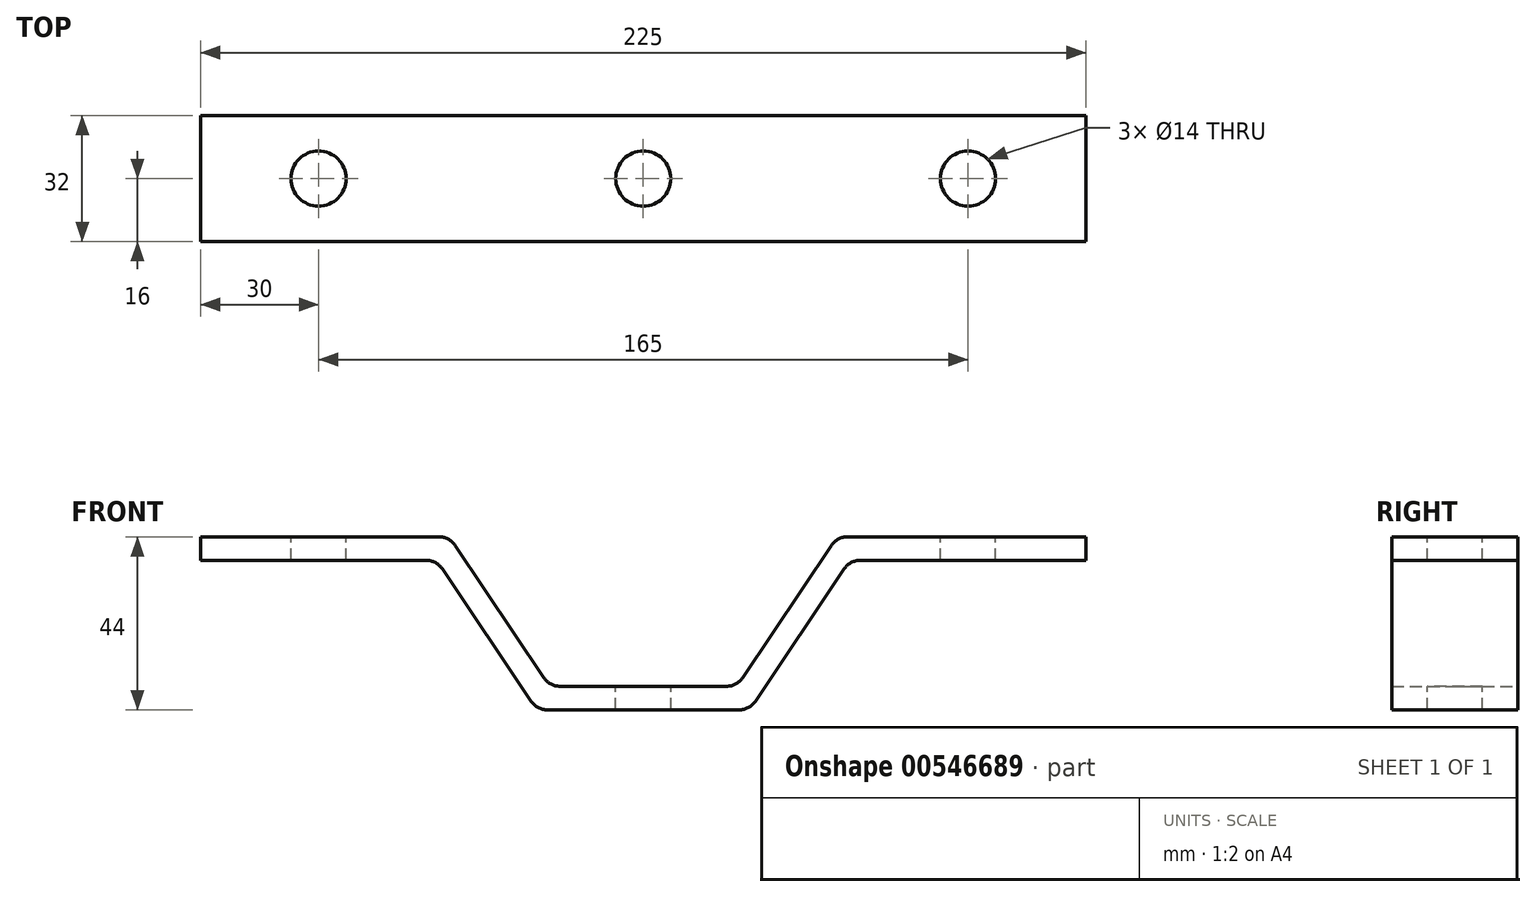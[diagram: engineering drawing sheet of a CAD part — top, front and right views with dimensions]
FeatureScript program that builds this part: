
annotation { "Feature Type Name" : "Feature", "Feature Type Description" : "" }
export const myFeature = defineFeature(function(context is Context, id is Id, definition is map)
    precondition{}
    {
        {
            var Q0;
            Q0=qCreatedBy(makeId("Front.planeOp"),FACE);
            var sketch = newSketch(context, id + "F0", { "sketchPlane" : qUnion([Q0])});
            skLineSegment(sketch, "E0", {"start": v(-27, 0) * mm, "end": v(27, 0) * mm});
            skLineSegment(sketch, "E1", {"start": v(-52.5, 38) * mm, "end": v(-112.5, 38) * mm});
            skLineSegment(sketch, "E2", {"start": v(52.5, 38) * mm, "end": v(112.5, 38) * mm});
            skLineSegment(sketch, "E3", {"start": v(-52.5, 38) * mm, "end": v(-27, 0) * mm});
            skLineSegment(sketch, "E4", {"start": v(27, 0) * mm, "end": v(52.5, 38) * mm});
            skLineSegment(sketch, "E5", {"start": v(-112.5, 38) * mm, "end": v(-112.5, 44) * mm});
            skLineSegment(sketch, "E6", {"start": v(112.5, 38) * mm, "end": v(112.5, 44) * mm});
            skLineSegment(sketch, "E7", {"start": v(-112.5, 44) * mm, "end": v(-49.3, 44) * mm});
            skLineSegment(sketch, "E8", {"start": v(-49.3, 44) * mm, "end": v(-23.8, 6) * mm});
            skLineSegment(sketch, "E9", {"start": v(-23.8, 6) * mm, "end": v(23.8, 6) * mm});
            skLineSegment(sketch, "E10", {"start": v(23.8, 6) * mm, "end": v(49.3, 44) * mm});
            skLineSegment(sketch, "E11", {"start": v(49.3, 44) * mm, "end": v(112.5, 44) * mm});
            skSolve(sketch);
        }
        {
            var Q0;
            Q0=makeQuery(id+"F0.imprint","IMPRINT",FACE,{"disambiguationData":[TD([[makeQuery(id+"F0.imprint","IMPRINT",EDGE,{"derivedFrom":sQuery(id+"F0.wireOp",EDGE,"E0")}),1.0]])]});
            extrude(context, id + "F1", {"entities" : qUnion([Q0]), "depth" : 32 * mm, "offsetDistance" : 25 * mm});
        }
        {
            var Q0;
            Q0=makeQuery(id+"F1.opExtrude","SWEPT_EDGE",EDGE,{"disambiguationData":[OSD([sQuery(id+"F0.wireOp",EDGE,"E7"),sQuery(id+"F0.wireOp",EDGE,"E8")])]});
            var Q1;
            Q1=makeQuery(id+"F1.opExtrude","SWEPT_EDGE",EDGE,{"disambiguationData":[OSD([sQuery(id+"F0.wireOp",EDGE,"E8"),sQuery(id+"F0.wireOp",EDGE,"E9")])]});
            var Q2;
            Q2=makeQuery(id+"F1.opExtrude","SWEPT_EDGE",EDGE,{"disambiguationData":[OSD([sQuery(id+"F0.wireOp",EDGE,"E9"),sQuery(id+"F0.wireOp",EDGE,"E10")])]});
            var Q3;
            Q3=makeQuery(id+"F1.opExtrude","SWEPT_EDGE",EDGE,{"disambiguationData":[OSD([sQuery(id+"F0.wireOp",EDGE,"E10"),sQuery(id+"F0.wireOp",EDGE,"E11")])]});
            var Q4;
            Q4=makeQuery(id+"F1.opExtrude","SWEPT_EDGE",EDGE,{"disambiguationData":[OSD([sQuery(id+"F0.wireOp",EDGE,"E2"),sQuery(id+"F0.wireOp",EDGE,"E4")])]});
            var Q5;
            Q5=makeQuery(id+"F1.opExtrude","SWEPT_EDGE",EDGE,{"disambiguationData":[OSD([sQuery(id+"F0.wireOp",EDGE,"E0"),sQuery(id+"F0.wireOp",EDGE,"E4")])]});
            var Q6;
            Q6=makeQuery(id+"F1.opExtrude","SWEPT_EDGE",EDGE,{"disambiguationData":[OSD([sQuery(id+"F0.wireOp",EDGE,"E0"),sQuery(id+"F0.wireOp",EDGE,"E3")])]});
            var Q7;
            Q7=makeQuery(id+"F1.opExtrude","SWEPT_EDGE",EDGE,{"disambiguationData":[OSD([sQuery(id+"F0.wireOp",EDGE,"E1"),sQuery(id+"F0.wireOp",EDGE,"E3")])]});
            fillet(context, id + "F2", {"entities" : qUnion([Q0, Q1, Q2, Q3, Q4, Q5, Q6, Q7]), "radius" : 5 * mm, "tangentPropagation" : true, "allowEdgeOverflow" : false});
        }
        {
            var Q0;
            Q0=makeQuery(id+"F1.opExtrude","SWEPT_FACE",FACE,{"disambiguationData":[OSD([sQuery(id+"F0.wireOp",EDGE,"E9")])]});
            var sketch = newSketch(context, id + "F3", { "sketchPlane" : qUnion([Q0])});
            skCircle(sketch, "E12", {"center": v(0, -16) * mm, "radius": 2.67 * mm});
            skSolve(sketch);
        }
        {
            var Q0;
            Q0=sQuery(id+"F3.wireOp",VERTEX,"E12.center");
            var Q1;
            Q1=makeQuery(id+"F1.opExtrude","SWEPT_BODY",BODY,{"disambiguationData":[OSD([sQuery(id+"F0.wireOp",EDGE,"E0"),sQuery(id+"F0.wireOp",EDGE,"E1"),sQuery(id+"F0.wireOp",EDGE,"E2"),sQuery(id+"F0.wireOp",EDGE,"E3"),sQuery(id+"F0.wireOp",EDGE,"E4"),sQuery(id+"F0.wireOp",EDGE,"E5"),sQuery(id+"F0.wireOp",EDGE,"E6"),sQuery(id+"F0.wireOp",EDGE,"E7"),sQuery(id+"F0.wireOp",EDGE,"E8"),sQuery(id+"F0.wireOp",EDGE,"E9"),sQuery(id+"F0.wireOp",EDGE,"E10"),sQuery(id+"F0.wireOp",EDGE,"E11")])]});
            hole(context, id + "F4", {"style" : HoleStyle.SIMPLE, "endStyle" : HoleEndStyle.THROUGH, "holeDiameter" : 14 * mm, "tappedDepth" : 12 * mm, "tapClearance" : 3, "locations" : qUnion([Q0]), "scope" : qUnion([Q1])});
        }
        {
            var Q0;
            Q0=makeQuery(id+"F1.opExtrude","SWEPT_FACE",FACE,{"disambiguationData":[OSD([sQuery(id+"F0.wireOp",EDGE,"E11")])]});
            var sketch = newSketch(context, id + "F5", { "sketchPlane" : qUnion([Q0])});
            skCircle(sketch, "E13", {"center": v(82.5, -16) * mm, "radius": 4.63 * mm});
            skCircle(sketch, "E14", {"center": v(-82.5, -16) * mm, "radius": 5.02 * mm});
            skSolve(sketch);
        }
        {
            var Q0;
            Q0=sQuery(id+"F5.wireOp",VERTEX,"E14.center");
            var Q1;
            Q1=sQuery(id+"F5.wireOp",VERTEX,"E13.center");
            var Q2;
            Q2=makeQuery(id+"F1.opExtrude","SWEPT_BODY",BODY,{"disambiguationData":[OSD([sQuery(id+"F0.wireOp",EDGE,"E0"),sQuery(id+"F0.wireOp",EDGE,"E1"),sQuery(id+"F0.wireOp",EDGE,"E2"),sQuery(id+"F0.wireOp",EDGE,"E3"),sQuery(id+"F0.wireOp",EDGE,"E4"),sQuery(id+"F0.wireOp",EDGE,"E5"),sQuery(id+"F0.wireOp",EDGE,"E6"),sQuery(id+"F0.wireOp",EDGE,"E7"),sQuery(id+"F0.wireOp",EDGE,"E8"),sQuery(id+"F0.wireOp",EDGE,"E9"),sQuery(id+"F0.wireOp",EDGE,"E10"),sQuery(id+"F0.wireOp",EDGE,"E11")])]});
            hole(context, id + "F6", {"style" : HoleStyle.SIMPLE, "endStyle" : HoleEndStyle.THROUGH, "holeDiameter" : 14 * mm, "tappedDepth" : 12 * mm, "tapClearance" : 3, "locations" : qUnion([Q0, Q1]), "scope" : qUnion([Q2])});
        }
    });
